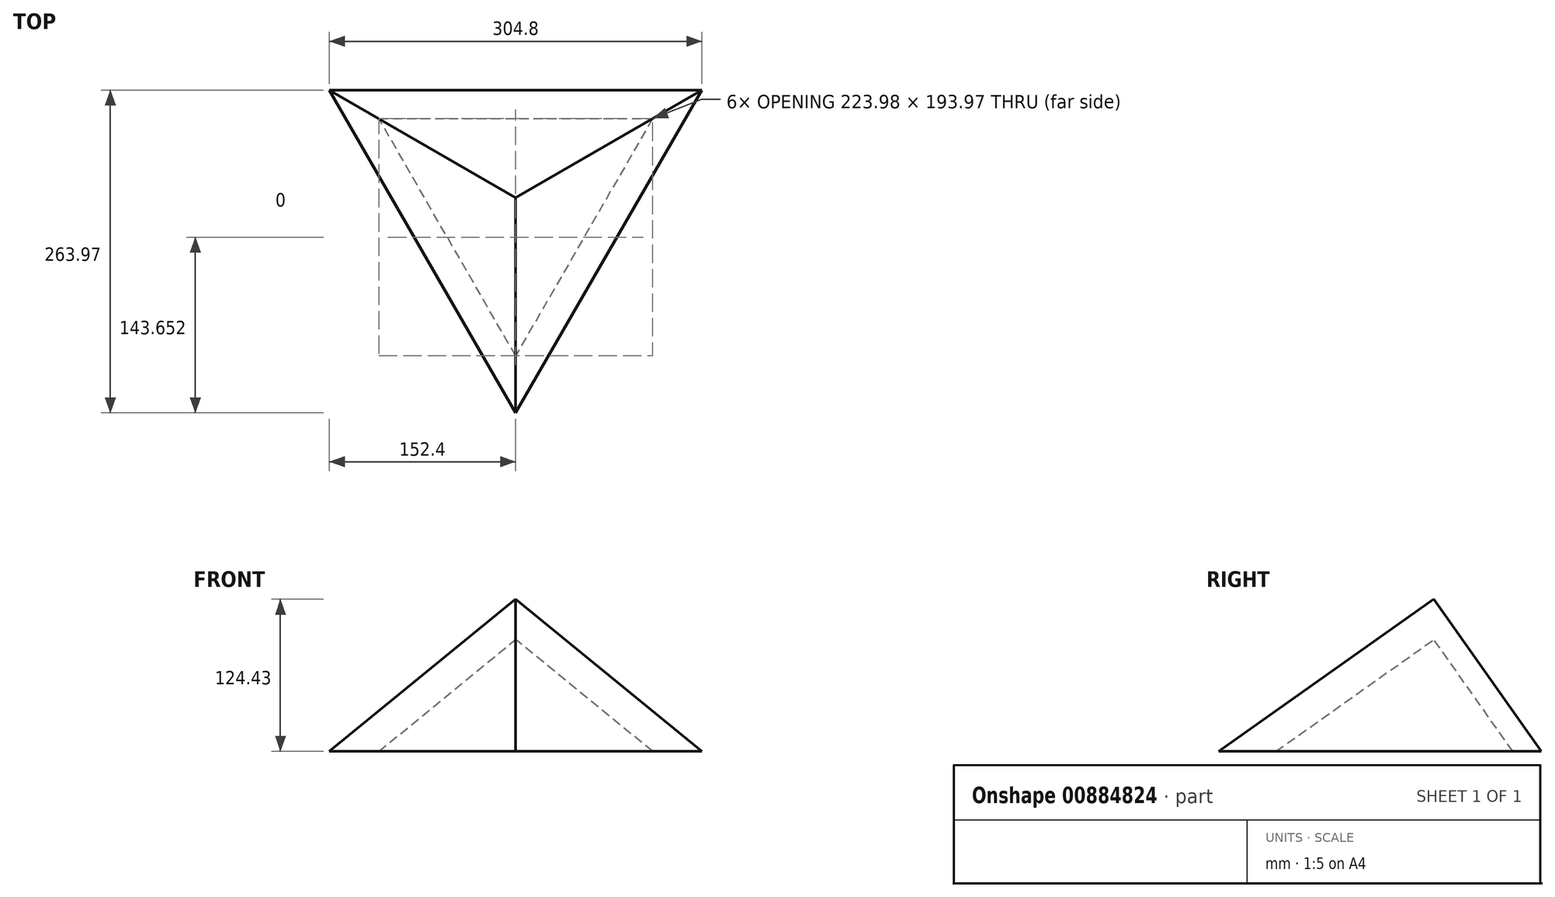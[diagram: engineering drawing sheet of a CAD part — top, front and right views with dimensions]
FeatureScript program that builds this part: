
annotation { "Feature Type Name" : "Feature", "Feature Type Description" : "" }
export const myFeature = defineFeature(function(context is Context, id is Id, definition is map)
    precondition{}
    {
        {
            var Q0;
            Q0=qCreatedBy(makeId("Top.planeOp"),FACE);
            var sketch = newSketch(context, id + "F0", { "sketchPlane" : qUnion([Q0])});
            skCircle(sketch, "E0.cCircle", {"center": v(0, 0) * mm, "radius": 87.99 * mm, "construction": true});
            skLineSegment(sketch, "E0.0", {"start": v(-152.4, 87.99) * mm, "end": v(152.4, 87.99) * mm});
            skLineSegment(sketch, "E0.1", {"start": v(152.4, 87.99) * mm, "end": v(0, -175.98) * mm});
            skLineSegment(sketch, "E0.2", {"start": v(0, -175.98) * mm, "end": v(-152.4, 87.99) * mm});
            skPoint(sketch, "E0.0.midPoint", {"position": v(0, 87.99) * mm});
            skSolve(sketch);
        }
        {
            var Q0;
            Q0=qCreatedBy(makeId("Front.planeOp"),FACE);
            var sketch = newSketch(context, id + "F1", { "sketchPlane" : qUnion([Q0])});
            skPoint(sketch, "E1", {"position": v(0, 124.43) * mm});
            skSolve(sketch);
        }
        {
            var Q0;
            Q0=makeQuery(id+"F0.imprint","IMPRINT",FACE,{"disambiguationData":[TD([[makeQuery(id+"F0.imprint","IMPRINT",EDGE,{"derivedFrom":sQuery(id+"F0.wireOp",EDGE,"E0.0")}),-1.0]])]});
            var Q1;
            Q1=sQuery(id+"F1.wireOp",VERTEX,"E1");
            loft(context, id + "F2", {"sheetProfilesArray" : [{ "sheetProfileEntities" : qUnion([Q0]) }, { "sheetProfileEntities" : qUnion([Q1]) }]});
        }
        {
            var Q0;
            Q0=makeQuery(id+"F2.opLoft","CAP_FACE",FACE,{"disambiguationData":[OSD([makeQuery(id+"F0.imprint","IMPRINT",FACE,{"disambiguationData":[TD([[makeQuery(id+"F0.imprint","IMPRINT",EDGE,{"derivedFrom":sQuery(id+"F0.wireOp",EDGE,"E0.0")}),-1.0]])]})])],"isStart":true});
            shell(context, id + "F3", {"entities" : qUnion([Q0]), "thickness" : 19.05 * mm});
        }
    });
